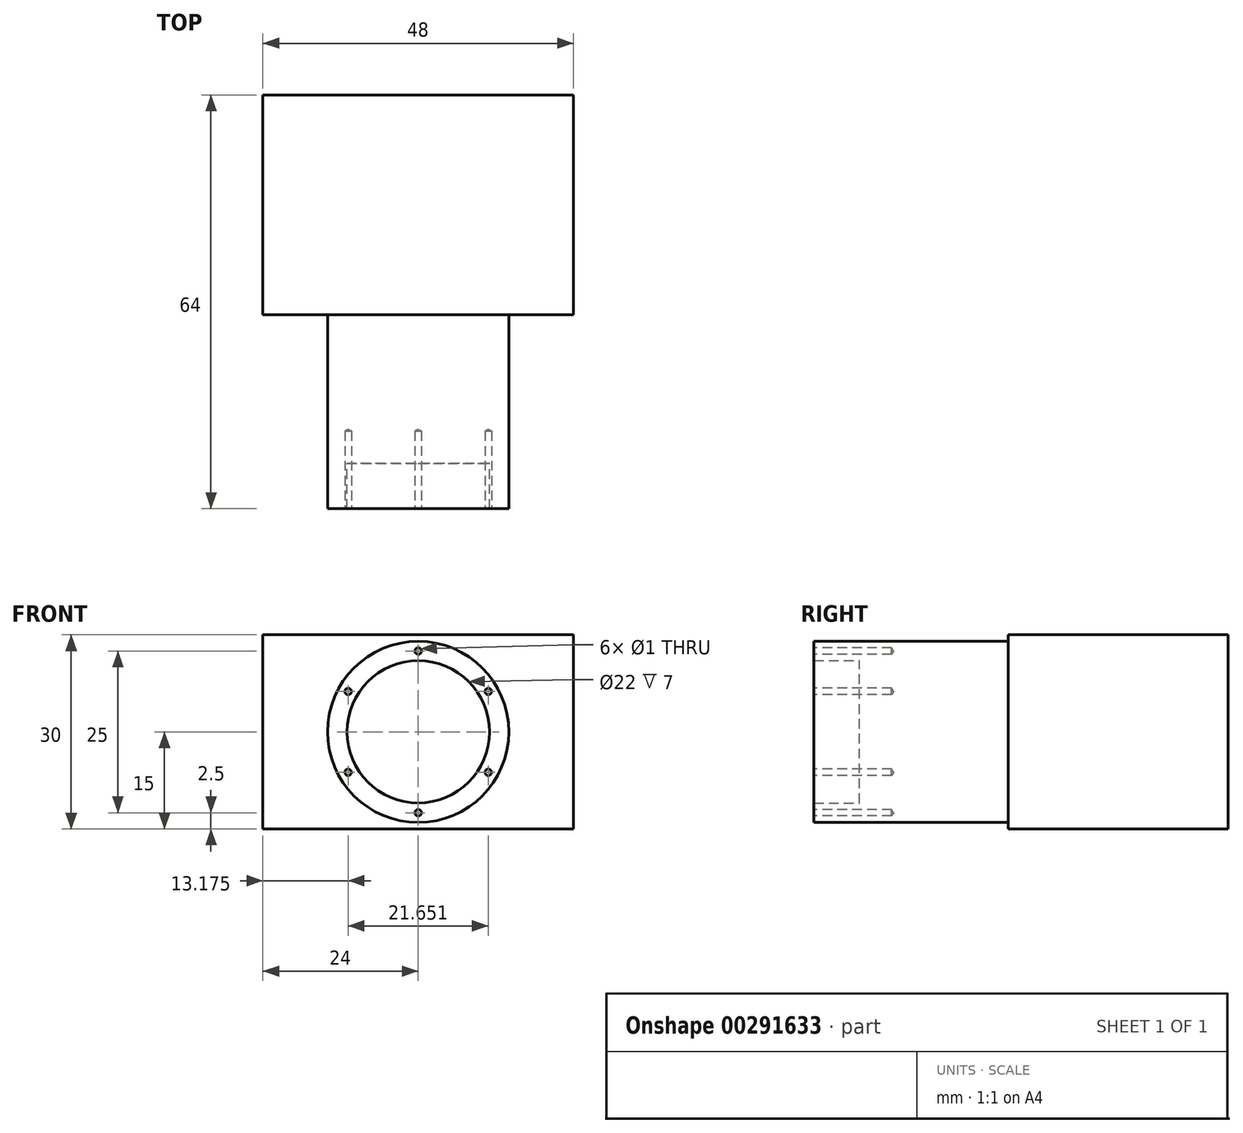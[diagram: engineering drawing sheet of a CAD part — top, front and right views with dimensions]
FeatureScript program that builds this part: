
annotation { "Feature Type Name" : "Feature", "Feature Type Description" : "" }
export const myFeature = defineFeature(function(context is Context, id is Id, definition is map)
    precondition{}
    {
        {
            var Q0;
            Q0=qCreatedBy(makeId("Front.planeOp"),FACE);
            var sketch = newSketch(context, id + "F0", { "sketchPlane" : qUnion([Q0])});
            skLineSegment(sketch, "E0.bottom", {"start": v(24, -15) * mm, "end": v(-24, -15) * mm});
            skLineSegment(sketch, "E0.top", {"start": v(24, 15) * mm, "end": v(-24, 15) * mm});
            skLineSegment(sketch, "E0.left", {"start": v(24, -15) * mm, "end": v(24, 15) * mm});
            skLineSegment(sketch, "E0.right", {"start": v(-24, -15) * mm, "end": v(-24, 15) * mm});
            skPoint(sketch, "E0.middle", {"position": v(0, 0) * mm});
            skSolve(sketch);
        }
        {
            var Q0;
            Q0=makeQuery(id+"F0.imprint","IMPRINT",FACE,{"disambiguationData":[TD([[makeQuery(id+"F0.imprint","IMPRINT",EDGE,{"derivedFrom":sQuery(id+"F0.wireOp",EDGE,"E0.bottom")}),-1.0]])]});
            extrude(context, id + "F1", {"entities" : qUnion([Q0]), "depth" : 34 * mm});
        }
        {
            var Q0;
            Q0=makeQuery(id+"F1.opExtrude","CAP_FACE",FACE,{"disambiguationData":[OSD([sQuery(id+"F0.wireOp",EDGE,"E0.bottom"),sQuery(id+"F0.wireOp",EDGE,"E0.top"),sQuery(id+"F0.wireOp",EDGE,"E0.left"),sQuery(id+"F0.wireOp",EDGE,"E0.right")])],"isStart":false});
            var sketch = newSketch(context, id + "F2", { "sketchPlane" : qUnion([Q0])});
            skCircle(sketch, "E1", {"center": v(0, 0) * mm, "radius": 14 * mm});
            skCircle(sketch, "E2", {"center": v(0, 0) * mm, "radius": 11 * mm});
            skSolve(sketch);
        }
        {
            var Q0;
            Q0=makeQuery(id+"F2.imprint","IMPRINT",FACE,{"disambiguationData":[TD([[makeQuery(id+"F2.imprint","IMPRINT",EDGE,{"derivedFrom":sQuery(id+"F2.wireOp",EDGE,"E1")}),1.0]])]});
            extrude(context, id + "F3", {"entities" : qUnion([Q0]), "operationType" : NewBodyOperationType.ADD, "depth" : 30 * mm});
        }
        {
            var Q0;
            Q0=makeQuery(id+"F3.boolean.opBoolean","SPLIT",FACE,{"disambiguationData":[TD([makeQuery(id+"F3.opExtrude","SWEPT_FACE",FACE,{"disambiguationData":[OSD([sQuery(id+"F2.wireOp",EDGE,"E2")])]})])],"derivedFrom":makeQuery(id+"F1.opExtrude","CAP_FACE",FACE,{"disambiguationData":[OSD([sQuery(id+"F0.wireOp",EDGE,"E0.bottom"),sQuery(id+"F0.wireOp",EDGE,"E0.top"),sQuery(id+"F0.wireOp",EDGE,"E0.left"),sQuery(id+"F0.wireOp",EDGE,"E0.right")])],"isStart":false})});
            extrude(context, id + "F4", {"entities" : qUnion([Q0]), "operationType" : NewBodyOperationType.ADD, "depth" : 23 * mm});
        }
        {
            var Q0;
            Q0=makeQuery(id+"F3.opExtrude","CAP_FACE",FACE,{"disambiguationData":[OSD([sQuery(id+"F2.wireOp",EDGE,"E1"),sQuery(id+"F2.wireOp",EDGE,"E2")])],"isStart":false});
            var sketch = newSketch(context, id + "F5", { "sketchPlane" : qUnion([Q0])});
            skCircle(sketch, "E3", {"center": v(0, 0) * mm, "radius": 12.5 * mm});
            skCircle(sketch, "E4", {"center": v(0, 12.5) * mm, "radius": 0.5 * mm});
            skCircle(sketch, "E5.1.0", {"center": v(-10.83, 6.25) * mm, "radius": 0.5 * mm});
            skCircle(sketch, "E5.2.0", {"center": v(-10.83, -6.25) * mm, "radius": 0.5 * mm});
            skCircle(sketch, "E5.3.0", {"center": v(0, -12.5) * mm, "radius": 0.5 * mm});
            skCircle(sketch, "E5.4.0", {"center": v(10.83, -6.25) * mm, "radius": 0.5 * mm});
            skCircle(sketch, "E5.5.0", {"center": v(10.83, 6.25) * mm, "radius": 0.5 * mm});
            skSolve(sketch);
        }
        {
            var Q0;
            Q0=sQuery(id+"F5.wireOp",VERTEX,"E4.center");
            var Q1;
            Q1=sQuery(id+"F5.wireOp",VERTEX,"E5.1.0.center");
            var Q2;
            Q2=sQuery(id+"F5.wireOp",VERTEX,"E5.2.0.center");
            var Q3;
            Q3=sQuery(id+"F5.wireOp",VERTEX,"E5.3.0.center");
            var Q4;
            Q4=sQuery(id+"F5.wireOp",VERTEX,"E5.4.0.center");
            var Q5;
            Q5=sQuery(id+"F5.wireOp",VERTEX,"E5.5.0.center");
            var Q6;
            Q6=makeQuery(id+"F1.opExtrude","SWEPT_BODY",BODY,{"disambiguationData":[OSD([sQuery(id+"F0.wireOp",EDGE,"E0.bottom"),sQuery(id+"F0.wireOp",EDGE,"E0.top"),sQuery(id+"F0.wireOp",EDGE,"E0.left"),sQuery(id+"F0.wireOp",EDGE,"E0.right")])]});
            hole(context, id + "F6", {"style" : HoleStyle.SIMPLE, "endStyle" : HoleEndStyle.BLIND, "holeDiameter" : 1 * mm, "holeDepth" : 12 * mm, "tappedDepth" : 12 * mm, "tapClearance" : 3, "startFromSketch" : true, "locations" : qUnion([Q0, Q1, Q2, Q3, Q4, Q5]), "scope" : qUnion([Q6])});
        }
    });
